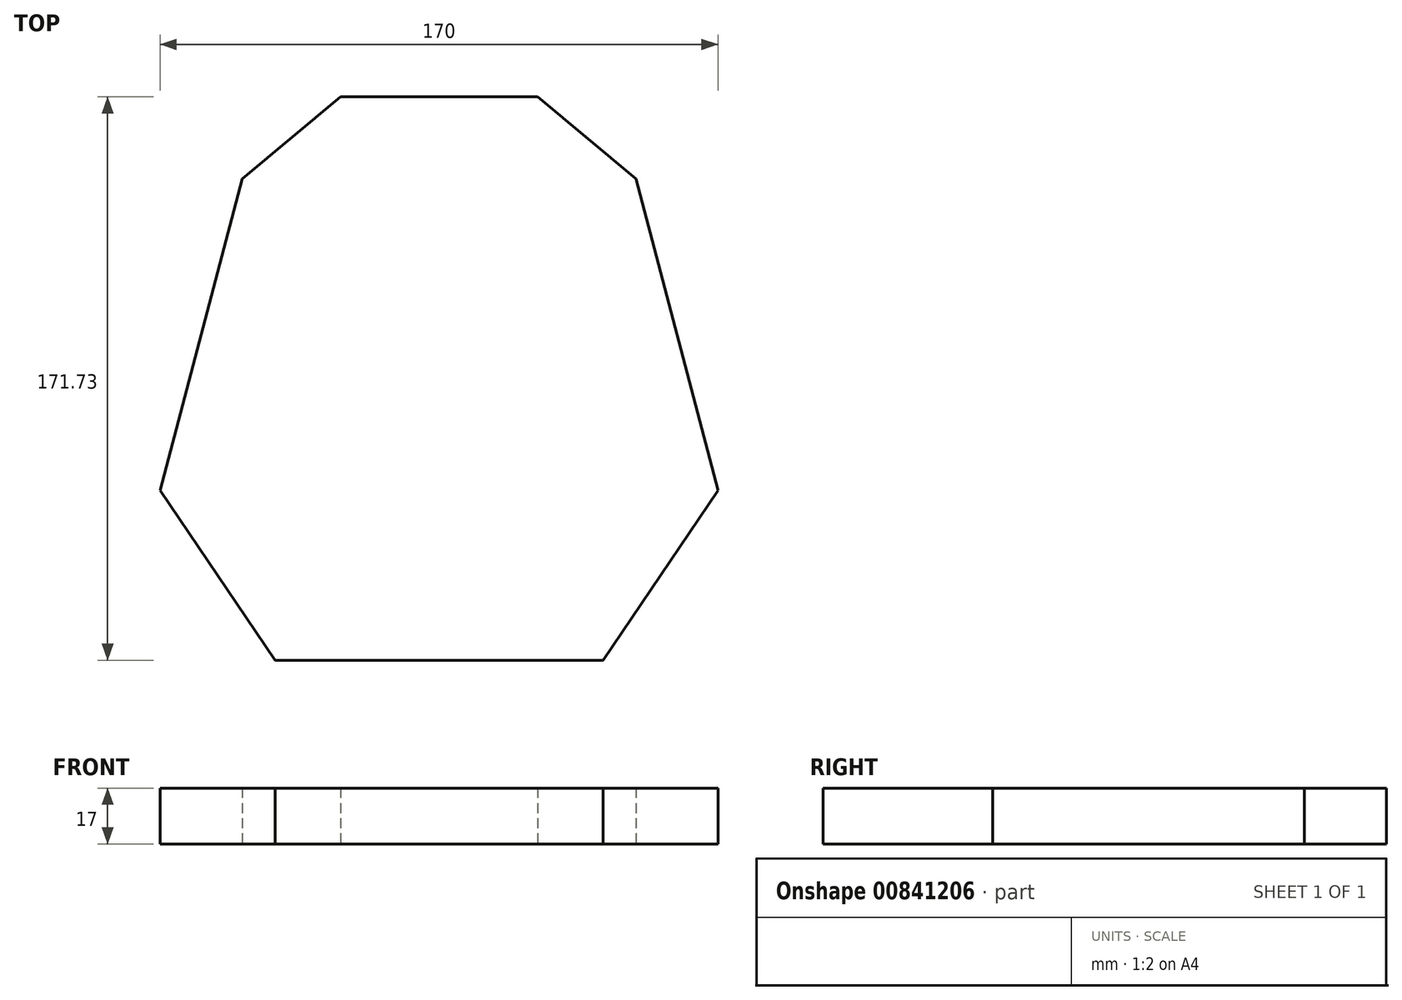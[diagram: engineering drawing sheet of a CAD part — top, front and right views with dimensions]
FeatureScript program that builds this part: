
annotation { "Feature Type Name" : "Feature", "Feature Type Description" : "" }
export const myFeature = defineFeature(function(context is Context, id is Id, definition is map)
    precondition{}
    {
        {
            var Q0;
            Q0=qCreatedBy(makeId("Top.planeOp"),FACE);
            var sketch = newSketch(context, id + "F0", { "sketchPlane" : qUnion([Q0])});
            skLineSegment(sketch, "E0", {"start": v(-231.89, -166.17) * mm, "end": v(-201.89, -191.17) * mm});
            skLineSegment(sketch, "E1", {"start": v(-201.89, -191.17) * mm, "end": v(-141.89, -191.17) * mm});
            skLineSegment(sketch, "E2", {"start": v(-141.89, -191.17) * mm, "end": v(-111.89, -166.17) * mm});
            skLineSegment(sketch, "E3", {"start": v(-111.89, -166.17) * mm, "end": v(-86.89, -71.17) * mm});
            skLineSegment(sketch, "E4", {"start": v(-86.89, -71.17) * mm, "end": v(-121.89, -19.45) * mm});
            skLineSegment(sketch, "E5", {"start": v(-121.89, -19.45) * mm, "end": v(-221.89, -19.45) * mm});
            skLineSegment(sketch, "E6", {"start": v(-221.89, -19.45) * mm, "end": v(-256.89, -71.17) * mm});
            skLineSegment(sketch, "E7", {"start": v(-256.89, -71.17) * mm, "end": v(-231.89, -166.17) * mm});
            skLineSegment(sketch, "E8", {"start": v(-171.89, -191.17) * mm, "end": v(-171.89, -19.45) * mm, "construction": true});
            skSolve(sketch);
        }
        {
            var Q0;
            Q0=makeQuery(id+"F0.imprint","IMPRINT",FACE,{"disambiguationData":[TD([[makeQuery(id+"F0.imprint","IMPRINT",EDGE,{"derivedFrom":sQuery(id+"F0.wireOp",EDGE,"E0")}),1.0]])]});
            extrude(context, id + "F1", {"entities" : qUnion([Q0]), "depth" : 17 * mm, "offsetDistance" : 25 * mm});
        }
        {
            var Q0;
            Q0=makeQuery(id+"F1.opExtrude","SWEPT_BODY",BODY,{"disambiguationData":[OSD([sQuery(id+"F0.wireOp",EDGE,"E0"),sQuery(id+"F0.wireOp",EDGE,"E1"),sQuery(id+"F0.wireOp",EDGE,"E2"),sQuery(id+"F0.wireOp",EDGE,"E3"),sQuery(id+"F0.wireOp",EDGE,"E4"),sQuery(id+"F0.wireOp",EDGE,"E5"),sQuery(id+"F0.wireOp",EDGE,"E6"),sQuery(id+"F0.wireOp",EDGE,"E7")])]});
            var Q1;
            Q1=makeQuery(id+"F1.opExtrude","SWEPT_EDGE",EDGE,{"disambiguationData":[OSD([sQuery(id+"F0.wireOp",EDGE,"E1"),sQuery(id+"F0.wireOp",EDGE,"E2")])]});
            transform(context, id + "F2", {"entities" : qUnion([Q0]), "transformType" : TransformType.ROTATION, "transformAxis" : qUnion([Q1]), "angle" : 180 * degree, "makeCopy" : false});
        }
    });
